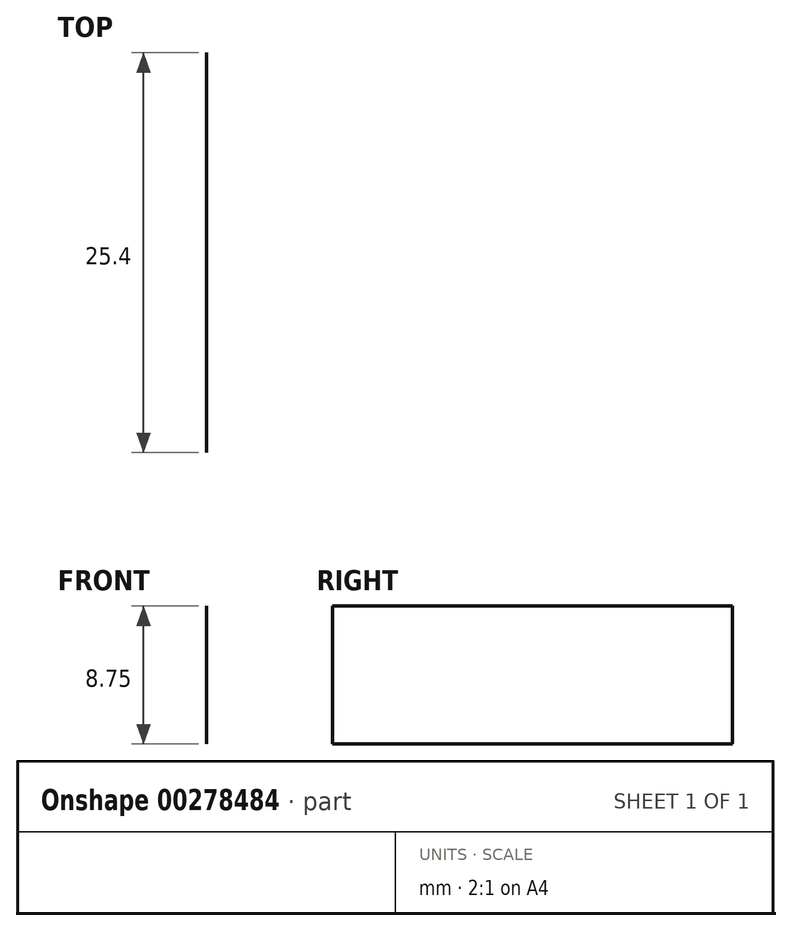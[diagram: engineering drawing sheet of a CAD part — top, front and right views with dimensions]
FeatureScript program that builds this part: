
annotation { "Feature Type Name" : "Feature", "Feature Type Description" : "" }
export const myFeature = defineFeature(function(context is Context, id is Id, definition is map)
    precondition{}
    {
        {
            var Q0;
            Q0=qCreatedBy(makeId("Front.planeOp"),FACE);
            var sketch = newSketch(context, id + "F0", { "sketchPlane" : qUnion([Q0])});
            skLineSegment(sketch, "E0.bottom", {"start": v(-68.04, -14.11) * mm, "end": v(68.04, -14.11) * mm});
            skLineSegment(sketch, "E0.top", {"start": v(-68.04, 14.11) * mm, "end": v(68.04, 14.11) * mm});
            skLineSegment(sketch, "E0.left", {"start": v(-68.04, -14.11) * mm, "end": v(-68.04, 14.11) * mm});
            skLineSegment(sketch, "E0.right", {"start": v(68.04, -14.11) * mm, "end": v(68.04, 14.11) * mm});
            skPoint(sketch, "E0.middle", {"position": v(0, 0) * mm});
            skLineSegment(sketch, "E1.bottom", {"start": v(127.33, 72.3) * mm, "end": v(133.9, 72.3) * mm});
            skLineSegment(sketch, "E1.top", {"start": v(127.33, 81.06) * mm, "end": v(133.9, 81.06) * mm});
            skLineSegment(sketch, "E1.left", {"start": v(127.33, 72.3) * mm, "end": v(127.33, 81.06) * mm});
            skLineSegment(sketch, "E1.right", {"start": v(133.9, 72.3) * mm, "end": v(133.9, 81.06) * mm});
            skSolve(sketch);
        }
        {
            var Q0;
            Q0=sQuery(id+"F0.wireOp",EDGE,"E1.right");
            extrude(context, id + "F1", {"bodyType" : ToolBodyType.SURFACE, "surfaceEntities" : qUnion([Q0]), "depth" : 25.4 * mm});
        }
    });
